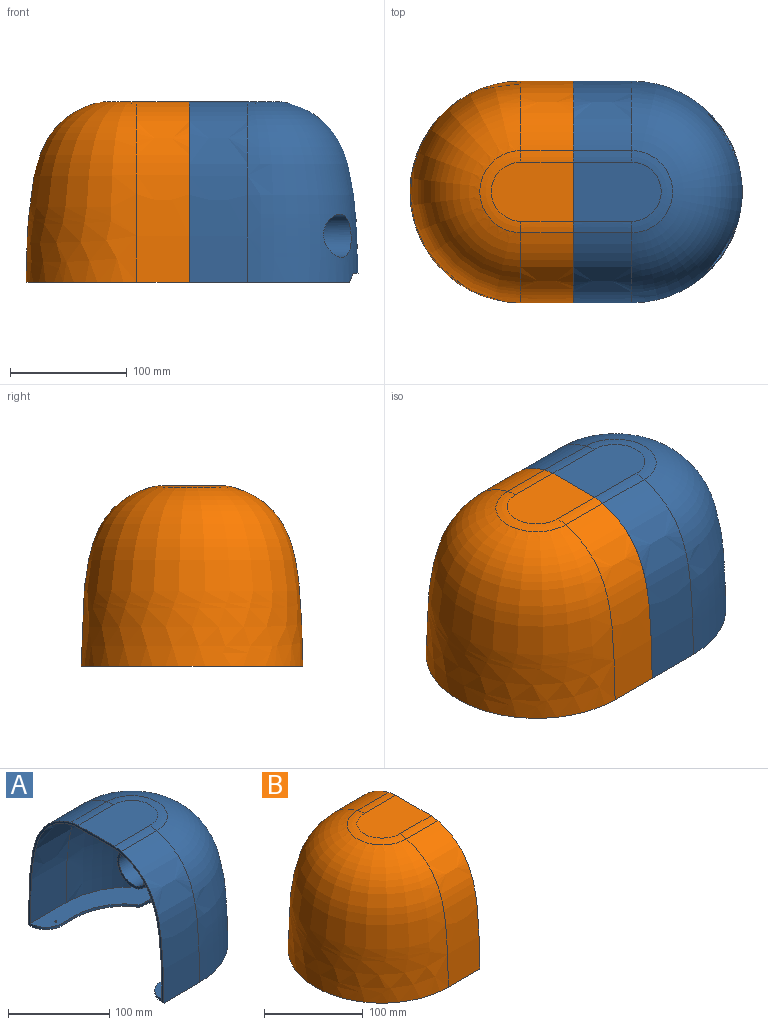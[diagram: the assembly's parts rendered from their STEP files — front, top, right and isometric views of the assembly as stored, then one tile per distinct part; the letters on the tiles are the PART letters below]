
ASSEMBLY  parts=2 mates=1
PART A: 41 faces, bbox 145.1x190.1x155.1 mm
  f0: plane 137.07x57mm, normal (0,0,-1), area 3723.6mm2, adj f15,f20,f25,f26,f35,f36,f37,f40
  f1: plane 134.03x54.54mm, normal (0,0,1), area 3269mm2, adj f7,f19,f25,f29,f35,f36,f37,f40
  f2: plane 56x37.82mm, normal (0,0,1), area 1817mm2, adj f7,f29,f31,f35
  f3: cylinder r=18.5mm len=38.78mm, axis (-1,0,0), area 3298.4mm2, adj f15,f32
  f4: cylinder r=18.5mm len=38.78mm, axis (-1,0,0), area 3299.3mm2, adj f15,f33
  f5: cylinder r=21.5mm len=43mm, axis (-1,0,0), area 3346.9mm2, adj f7,f33
  f6: cylinder r=21.5mm len=43mm, axis (-1,0,0), area 3346.7mm2, adj f7,f32
  f7: revolved ~183.99x145.21mm, area 37326.2mm2, adj f1,f2,f5,f6,f8,f14,f19,f29
  f8: extruded ~145.21x50mm, area 8146.5mm2, adj f7,f24,f25,f30
  f9: plane 137.07x57mm, normal (0,0,-1), area 3723.6mm2, adj f15,f23,f25,f28,f34,f35,f38,f39
  f10: revolved ~70.28x35.14mm, area 944.2mm2, adj f11,f15,f21,f22
  f11: plane 75.32x50.64mm, normal (0,0,1), area 3538.6mm2, adj f10,f21,f22,f25
  f12: plane 80x60mm, normal (0,0,-1), area 4413.7mm2, adj f13,f16,f17,f25
  f13: revolved ~71.4x35.7mm, area 603.4mm2, adj f12,f14,f16,f17
  f14: revolved ~86.82x43.41mm, area 1006.9mm2, adj f7,f13,f18,f24
  f15: revolved ~190x153.65mm, area 42315.1mm2, adj f0,f3,f4,f9,f10,f20,f23,f26
  f16: extruded ~50x5.7mm, area 292.3mm2, adj f12,f13,f24,f25
  f17: extruded ~50x5.7mm, area 292.3mm2, adj f12,f13,f18,f25
  f18: extruded ~50x7.71mm, area 405.2mm2, adj f14,f17,f19,f25
  f19: extruded ~145.21x50mm, area 8146.5mm2, adj f1,f7,f18,f25
  f20: extruded ~153.65x59.86mm, area 8939.8mm2, adj f0,f15,f21,f25
  f21: extruded ~50x9.82mm, area 496.7mm2, adj f10,f11,f20,f25
  f22: extruded ~50x9.82mm, area 496.7mm2, adj f10,f11,f23,f25
  f23: extruded ~153.65x59.86mm, area 8939.8mm2, adj f9,f15,f22,f25
  f24: extruded ~50x7.71mm, area 405.2mm2, adj f8,f14,f16,f25
  f25: plane 190x155mm, normal (-1,0,0), area 1135.3mm2, adj f0,f1,f8,f9,f11,f12,f16,f17
  f26: plane 41.85x10.09mm, normal (0,0.62,-0.78), area 477.2mm2, adj f0,f15,f27,f35
  f27: plane 56x40.62mm, normal (0,0,-1), area 1976.6mm2, adj f15,f26,f28,f35
  f28: plane 41.85x10.09mm, normal (0,-0.62,-0.78), area 477.2mm2, adj f9,f15,f27,f35
  f29: plane 38.56x9.55mm, normal (0,-0.65,0.76), area 422.5mm2, adj f1,f2,f7,f35
  f30: plane 134.03x54.54mm, normal (0,0,1), area 3269mm2, adj f7,f8,f25,f31,f34,f35,f38,f39
  f31: plane 38.56x9.55mm, normal (0,0.65,0.76), area 422.5mm2, adj f2,f7,f30,f35
  f32: plane 43x43mm, normal (-1,0,0), area 377mm2, adj f3,f6
  f33: plane 43x43mm, normal (-1,0,0), area 377mm2, adj f4,f5
  f34: plane 19x3mm, normal (0,-1,0), area 57mm2, adj f9,f30,f35,f39
  f35: cylinder r=70mm len=140mm, axis (0,0,1), area 654.7mm2, adj f0,f1,f2,f9,f26,f27,f28,f29
  f36: plane 19x3mm, normal (0,1,0), area 57mm2, adj f0,f1,f35,f40
  f37: cylinder r=1mm len=3mm, axis (0,0,-1), area 18.8mm2, adj f0,f1
  f38: cylinder r=1mm len=3mm, axis (0,0,-1), area 18.8mm2, adj f9,f30
  f39: cylinder r=21mm len=21mm, axis (0,0,1), area 99mm2, adj f9,f25,f30,f34
  f40: cylinder r=21mm len=21mm, axis (0,0,-1), area 99mm2, adj f0,f1,f25,f36
PART B: 23 faces, bbox 140x190x155 mm
  f0: plane 190x140mm, normal (0,0,-1), area 1903mm2, adj f2,f4,f10,f13,f20,f21,f22
  f1: plane 183.99x137mm, normal (0,0,1), area 750.6mm2, adj f2,f3,f14,f19,f20,f21,f22
  f2: plane 190x155mm, normal (1,0,0), area 1141.3mm2, adj f0,f1,f7,f8,f10,f11,f12,f13
  f3: revolved ~183.99x145.21mm, area 41394.1mm2, adj f1,f5,f14,f19
  f4: revolved ~190x153.65mm, area 45424mm2, adj f0,f9,f10,f13
  f5: revolved ~86.82x43.41mm, area 1006.9mm2, adj f3,f6,f15,f18
  f6: revolved ~71.4x35.7mm, area 603.4mm2, adj f5,f7,f16,f17
  f7: plane 75x60mm, normal (0,0,-1), area 4113.7mm2, adj f2,f6,f16,f17
  f8: plane 70.32x50.64mm, normal (0,0,1), area 3285.4mm2, adj f2,f9,f11,f12
  f9: revolved ~70.28x35.14mm, area 944.2mm2, adj f4,f8,f11,f12
  f10: extruded ~153.65x59.86mm, area 8045.8mm2, adj f0,f2,f4,f11
  f11: extruded ~45x9.82mm, area 447.1mm2, adj f2,f8,f9,f10
  f12: extruded ~45x9.82mm, area 447.1mm2, adj f2,f8,f9,f13
  f13: extruded ~153.65x59.86mm, area 8045.8mm2, adj f0,f2,f4,f12
  f14: extruded ~145.21x48.59mm, area 7331.8mm2, adj f1,f2,f3,f15
  f15: extruded ~45x7.71mm, area 364.6mm2, adj f2,f5,f14,f16
  f16: extruded ~45x5.7mm, area 263.1mm2, adj f2,f6,f7,f15
  f17: extruded ~45x5.7mm, area 263.1mm2, adj f2,f6,f7,f18
  f18: extruded ~45x7.71mm, area 364.6mm2, adj f2,f5,f17,f19
  f19: extruded ~145.21x48.59mm, area 7331.8mm2, adj f1,f2,f3,f18
  f20: plane 45x3mm, normal (0,1,0), area 135mm2, adj f0,f1,f2,f21
  f21: cylinder r=90mm len=180mm, axis (0,0,-1), area 848.2mm2, adj f0,f1,f20,f22
  f22: plane 45x3mm, normal (0,-1,0), area 135mm2, adj f0,f1,f2,f21
PLACE A t=(81.31,-53.16,-198.68)mm
PLACE B t=(-13.69,-53.16,-198.68)mm
MATE fastened B.f2 <-> A.f25  axis (1,0,0) through (31.31,-100.66,-276.18)mm
